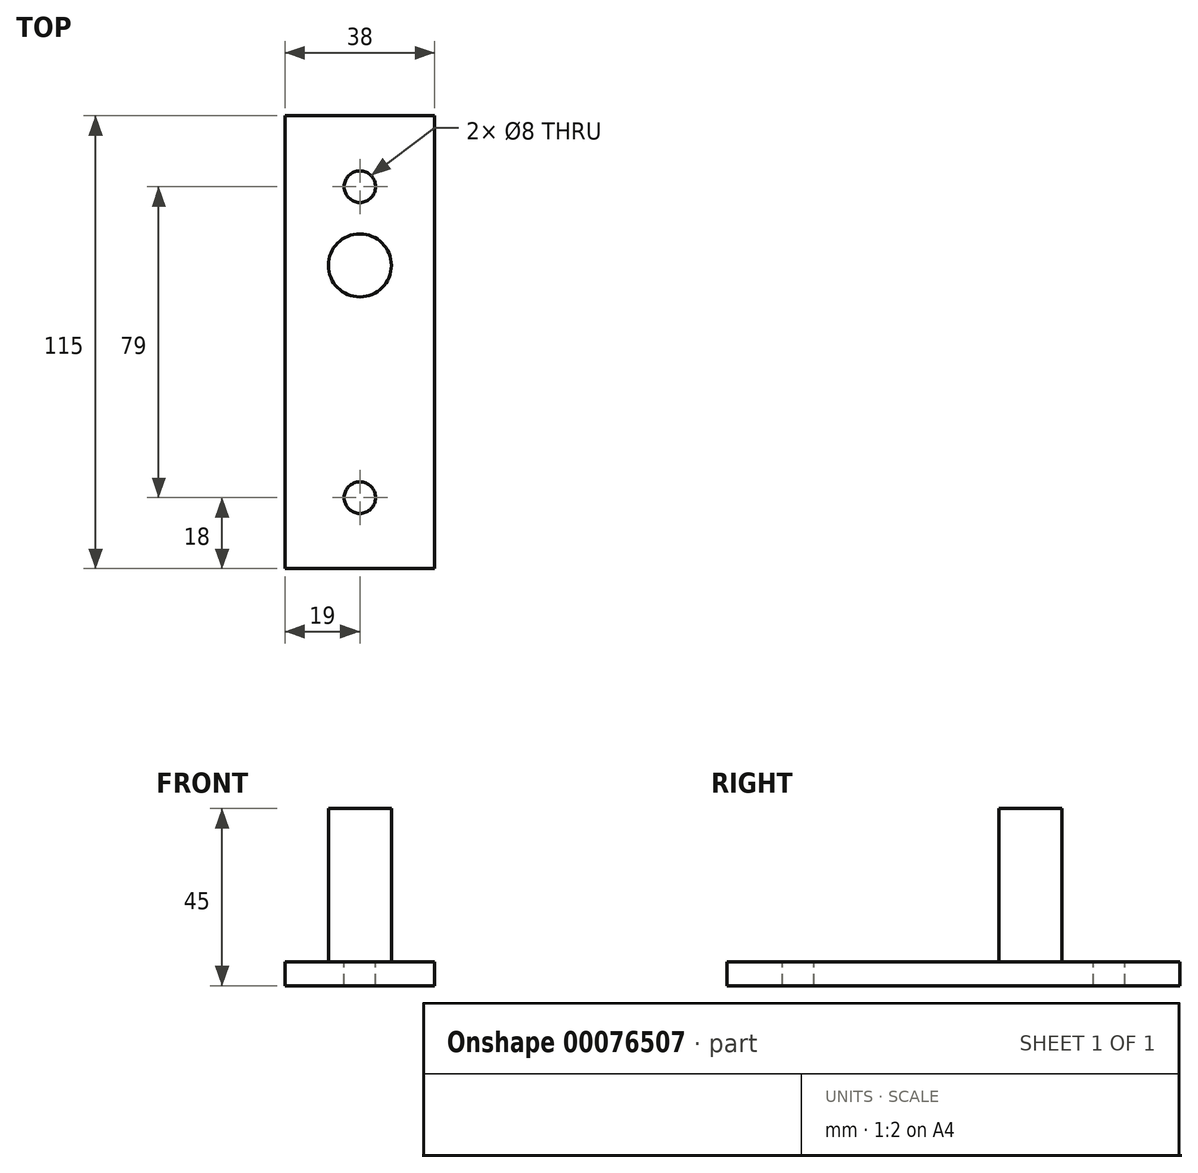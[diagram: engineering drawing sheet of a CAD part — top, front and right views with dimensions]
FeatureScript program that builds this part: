
annotation { "Feature Type Name" : "Feature", "Feature Type Description" : "" }
export const myFeature = defineFeature(function(context is Context, id is Id, definition is map)
    precondition{}
    {
        {
            var Q0;
            Q0=qCreatedBy(makeId("Front.planeOp"),FACE);
            var sketch = newSketch(context, id + "F0", { "sketchPlane" : qUnion([Q0])});
            skLineSegment(sketch, "E0.bottom", {"start": v(19, 3) * mm, "end": v(-19, 3) * mm});
            skLineSegment(sketch, "E0.top", {"start": v(19, -3) * mm, "end": v(-19, -3) * mm});
            skLineSegment(sketch, "E0.left", {"start": v(19, 3) * mm, "end": v(19, -3) * mm});
            skLineSegment(sketch, "E0.right", {"start": v(-19, 3) * mm, "end": v(-19, -3) * mm});
            skPoint(sketch, "E0.middle", {"position": v(0, 0) * mm});
            skSolve(sketch);
        }
        {
            var Q0;
            Q0 = qSketchRegion(id + "F0", true);
            extrude(context, id + "F1", {"entities" : qUnion([Q0]), "depth" : 57.5 * mm, "hasSecondDirection" : true, "secondDirectionOppositeDirection" : true, "secondDirectionDepth" : 57.5 * mm});
        }
        {
            var Q0;
            Q0=makeQuery(id+"F1.opExtrude","SWEPT_FACE",FACE,{"disambiguationData":[OSD([sQuery(id+"F0.wireOp",EDGE,"E0.bottom")])]});
            var sketch = newSketch(context, id + "F2", { "sketchPlane" : qUnion([Q0])});
            skCircle(sketch, "E1", {"center": v(0, 39.5) * mm, "radius": 4 * mm});
            skPoint(sketch, "E2.endSnap0", {"position": v(0, -57.5) * mm});
            skCircle(sketch, "E3", {"center": v(0, -39.5) * mm, "radius": 4 * mm});
            skSolve(sketch);
        }
        {
            var Q0;
            Q0 = qSketchRegion(id + "F2", true);
            extrude(context, id + "F3", {"entities" : qUnion([Q0]), "operationType" : NewBodyOperationType.REMOVE, "oppositeDirection" : true, "depth" : 6 * mm});
        }
        {
            var Q0;
            Q0=makeQuery(id+"F1.opExtrude","SWEPT_FACE",FACE,{"disambiguationData":[OSD([sQuery(id+"F0.wireOp",EDGE,"E0.bottom")])]});
            var sketch = newSketch(context, id + "F4", { "sketchPlane" : qUnion([Q0])});
            skCircle(sketch, "E4", {"center": v(0, 19.5) * mm, "radius": 8 * mm});
            skSolve(sketch);
        }
        {
            var Q0;
            Q0 = qSketchRegion(id + "F4", true);
            extrude(context, id + "F5", {"entities" : qUnion([Q0]), "operationType" : NewBodyOperationType.ADD, "depth" : 39 * mm});
        }
    });
